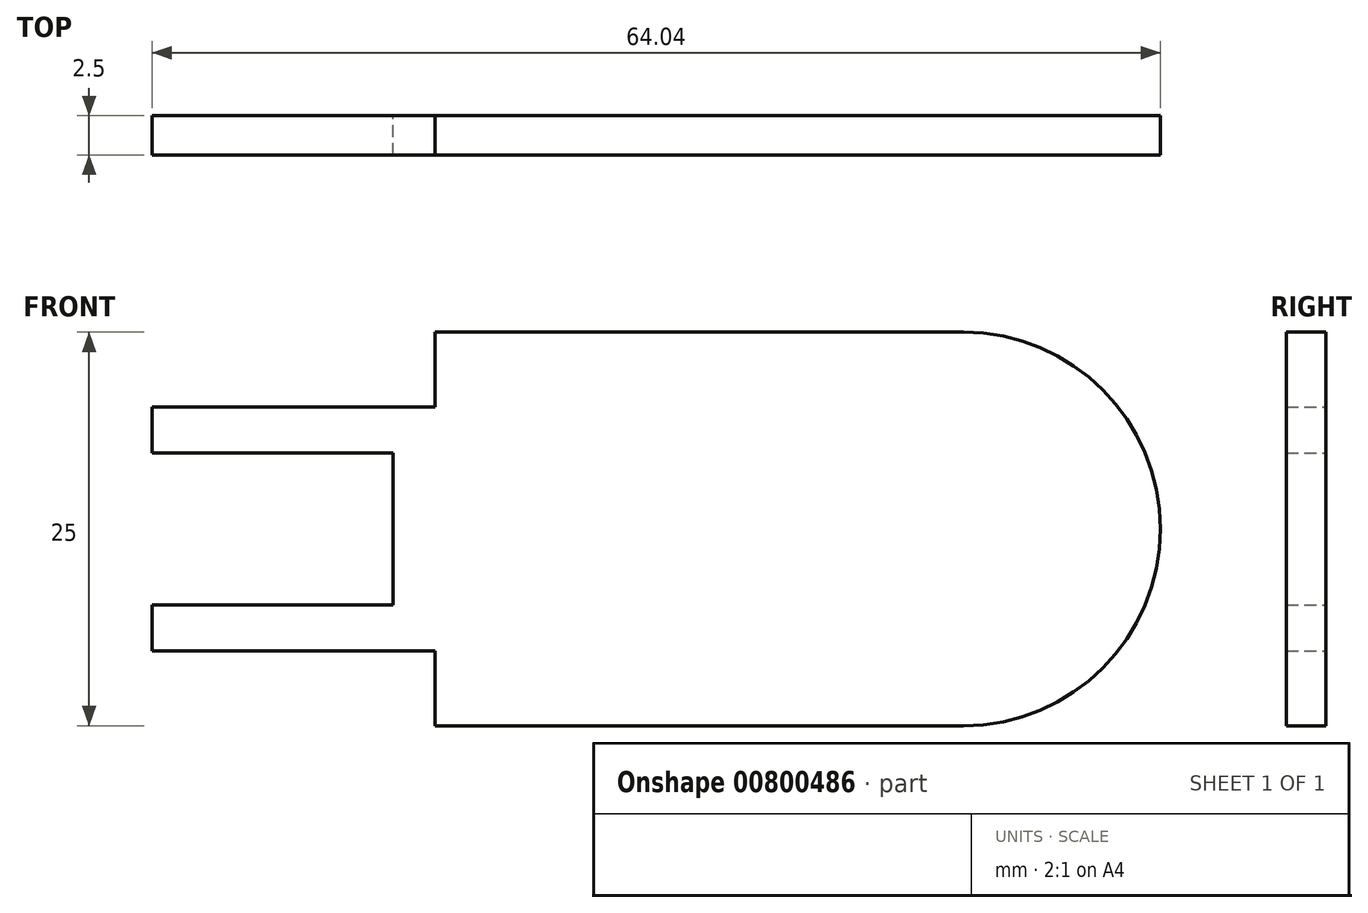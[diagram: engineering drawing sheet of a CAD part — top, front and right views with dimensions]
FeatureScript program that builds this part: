
annotation { "Feature Type Name" : "Feature", "Feature Type Description" : "" }
export const myFeature = defineFeature(function(context is Context, id is Id, definition is map)
    precondition{}
    {
        {
            var Q0;
            Q0=qCreatedBy(makeId("Front.planeOp"),FACE);
            var sketch = newSketch(context, id + "F0", { "sketchPlane" : qUnion([Q0])});
            skCircle(sketch, "E0", {"center": v(0, 0) * mm, "radius": 12.5 * mm});
            skLineSegment(sketch, "E1", {"start": v(0, 12.5) * mm, "end": v(-33.57, 12.5) * mm});
            skLineSegment(sketch, "E2", {"start": v(-33.57, 7.74) * mm, "end": v(-33.57, 12.5) * mm});
            skLineSegment(sketch, "E3.MirrorCS", {"start": v(-33.57, -7.74) * mm, "end": v(-33.57, -12.5) * mm});
            skLineSegment(sketch, "E4.MirrorCS", {"start": v(0, -12.5) * mm, "end": v(-33.57, -12.5) * mm});
            skLineSegment(sketch, "E5", {"start": v(-33.57, 7.74) * mm, "end": v(-51.54, 7.74) * mm});
            skLineSegment(sketch, "E6", {"start": v(-51.54, 7.74) * mm, "end": v(-51.54, 4.83) * mm});
            skLineSegment(sketch, "E7", {"start": v(-51.54, 4.83) * mm, "end": v(-36.25, 4.83) * mm});
            skLineSegment(sketch, "E8", {"start": v(-36.25, 4.83) * mm, "end": v(-36.25, 0) * mm});
            skLineSegment(sketch, "E9.MirrorCS", {"start": v(-36.25, -4.83) * mm, "end": v(-36.25, 0) * mm});
            skLineSegment(sketch, "E10.MirrorCS", {"start": v(-51.54, -4.83) * mm, "end": v(-36.25, -4.83) * mm});
            skLineSegment(sketch, "E11.MirrorCS", {"start": v(-51.54, -7.74) * mm, "end": v(-51.54, -4.83) * mm});
            skLineSegment(sketch, "E12.MirrorCS", {"start": v(-33.57, -7.74) * mm, "end": v(-51.54, -7.74) * mm});
            skSolve(sketch);
        }
        {
            var Q0;
            {var subQ1=sQuery(id+"F0.wireOp",EDGE,"E1");Q0=makeQuery(id+"F0.imprint","IMPRINT",FACE,{"disambiguationData":[TD([[makeQuery(id+"F0.imprint","IMPRINT",EDGE,{"derivedFrom":subQ1}),1.0]])]});}
            var Q1;
            {var subQ0=sQuery(id+"F0.wireOp",EDGE,"E0");var subQ1=makeQuery(id+"F0.imprint","INTERSECT",VERTEX,{"derivedFrom":[subQ0,sQuery(id+"F0.wireOp",EDGE,"E1")]});Q1=makeQuery(id+"F0.imprint","IMPRINT",FACE,{"disambiguationData":[TD([[makeQuery(id+"F0.imprint","IMPRINT",EDGE,{"disambiguationData":[TD([[subQ1,-1.0]])],"derivedFrom":subQ0}),1.0]])]});}
            extrude(context, id + "F1", {"entities" : qUnion([Q0, Q1]), "depth" : 2.5 * mm, "offsetDistance" : 25 * mm});
        }
    });
